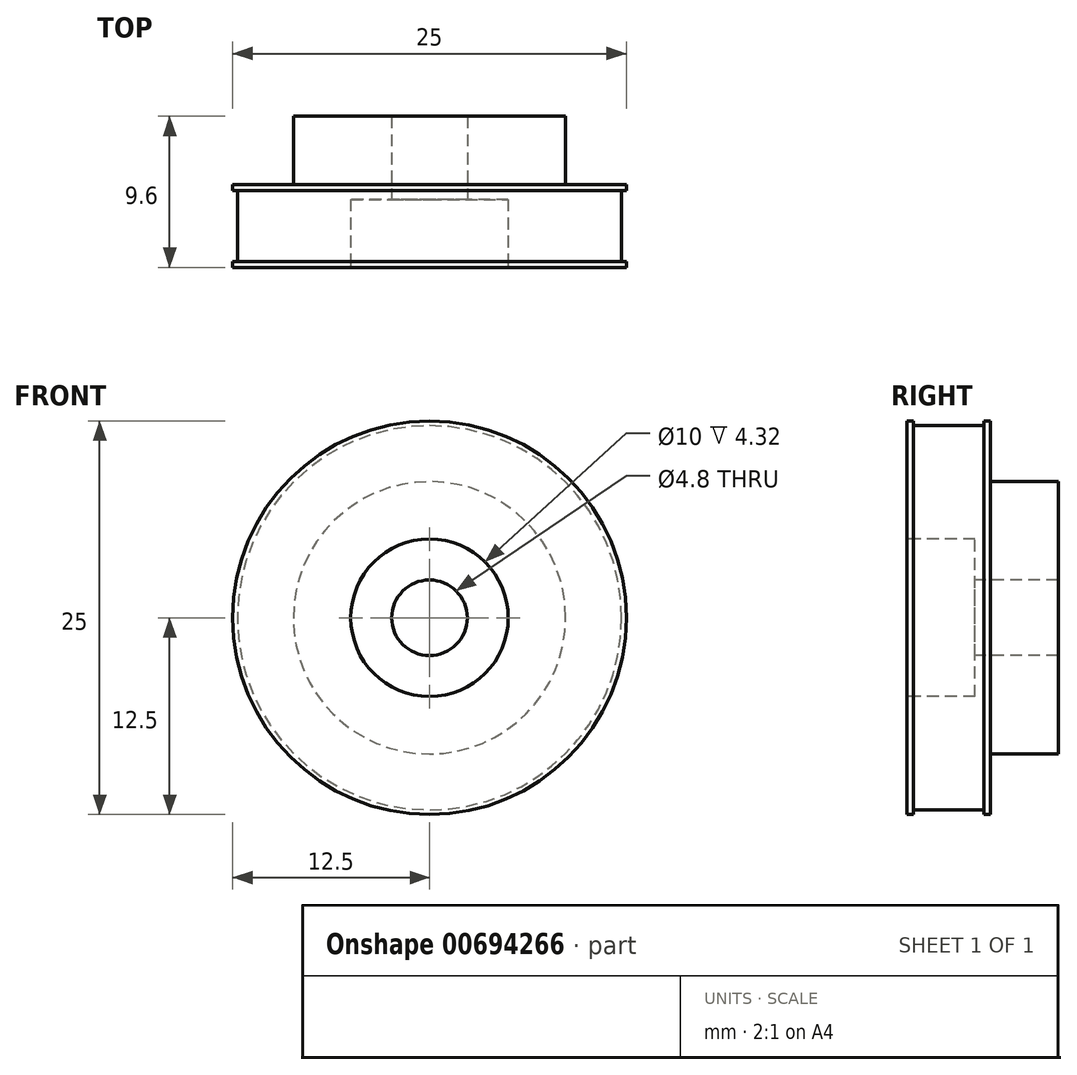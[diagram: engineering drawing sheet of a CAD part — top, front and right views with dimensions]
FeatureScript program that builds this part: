
annotation { "Feature Type Name" : "Feature", "Feature Type Description" : "" }
export const myFeature = defineFeature(function(context is Context, id is Id, definition is map)
    precondition{}
    {
        {
            var Q0;
            Q0=qCreatedBy(makeId("Front.planeOp"),FACE);
            var sketch = newSketch(context, id + "F0", { "sketchPlane" : qUnion([Q0])});
            skCircle(sketch, "E0", {"center": v(0, 0) * mm, "radius": 12.5 * mm});
            skSolve(sketch);
        }
        {
            var Q0;
            Q0=qSketchRegion(id+"F0",true);
            extrude(context, id + "F1", {"entities" : qUnion([Q0]), "depth" : 5.28 * mm, "offsetDistance" : 25 * mm});
        }
        {
            var Q0;
            Q0=makeQuery(id+"F1.opExtrude","CAP_FACE",FACE,{"disambiguationData":[OSD([sQuery(id+"F0.wireOp",EDGE,"E0")])],"isStart":true});
            var sketch = newSketch(context, id + "F2", { "sketchPlane" : qUnion([Q0])});
            skCircle(sketch, "E1", {"center": v(0, 0) * mm, "radius": 8.65 * mm});
            skSolve(sketch);
        }
        {
            var Q0;
            Q0=qSketchRegion(id+"F2",true);
            extrude(context, id + "F3", {"entities" : qUnion([Q0]), "operationType" : NewBodyOperationType.ADD, "depth" : 4.32 * mm, "offsetDistance" : 25 * mm});
        }
        {
            var Q0;
            Q0=makeQuery(id+"F1.opExtrude","CAP_FACE",FACE,{"disambiguationData":[OSD([sQuery(id+"F0.wireOp",EDGE,"E0")])],"isStart":false});
            var sketch = newSketch(context, id + "F4", { "sketchPlane" : qUnion([Q0])});
            skCircle(sketch, "E2", {"center": v(0, 0) * mm, "radius": 5 * mm});
            skSolve(sketch);
        }
        {
            var Q0;
            Q0=qSketchRegion(id+"F4",true);
            extrude(context, id + "F5", {"entities" : qUnion([Q0]), "operationType" : NewBodyOperationType.REMOVE, "oppositeDirection" : true, "depth" : 4.32 * mm, "offsetDistance" : 25 * mm});
        }
        {
            var Q0;
            Q0=qCreatedBy(makeId("Right.planeOp"),FACE);
            var sketch = newSketch(context, id + "F6", { "sketchPlane" : qUnion([Q0])});
            skLineSegment(sketch, "E3.bottom", {"start": v(-0.39, 12.5) * mm, "end": v(-4.9, 12.5) * mm});
            skLineSegment(sketch, "E3.top", {"start": v(-0.39, 12.2) * mm, "end": v(-4.9, 12.2) * mm});
            skLineSegment(sketch, "E3.left", {"start": v(-0.39, 12.5) * mm, "end": v(-0.39, 12.2) * mm});
            skLineSegment(sketch, "E3.right", {"start": v(-4.9, 12.5) * mm, "end": v(-4.9, 12.2) * mm});
            skSolve(sketch);
        }
        {
            var Q0;
            Q0=qSketchRegion(id+"F6",true);
            var Q1;
            Q1=makeQuery(id+"F1.opExtrude","SWEPT_FACE",FACE,{"disambiguationData":[OSD([sQuery(id+"F0.wireOp",EDGE,"E0")])]});
            revolve(context, id + "F7", {"operationType" : NewBodyOperationType.REMOVE, "entities" : qUnion([Q0]), "axis" : qUnion([Q1]), "revolveType" : RevolveType.FULL, "oppositeDirection" : true});
        }
        {
            var Q0;
            Q0=makeQuery(id+"F5.boolean.opBoolean","COPY",FACE,{"derivedFrom":makeQuery(id+"F5.opExtrude","CAP_FACE",FACE,{"disambiguationData":[OSD([sQuery(id+"F4.wireOp",EDGE,"E2")])],"isStart":false})});
            var sketch = newSketch(context, id + "F8", { "sketchPlane" : qUnion([Q0])});
            skCircle(sketch, "E4", {"center": v(0, 0) * mm, "radius": 2.4 * mm});
            skSolve(sketch);
        }
        {
            var Q0;
            Q0=qSketchRegion(id+"F8",true);
            extrude(context, id + "F9", {"entities" : qUnion([Q0]), "operationType" : NewBodyOperationType.REMOVE, "oppositeDirection" : true, "depth" : 25 * mm, "offsetDistance" : 25 * mm});
        }
    });
